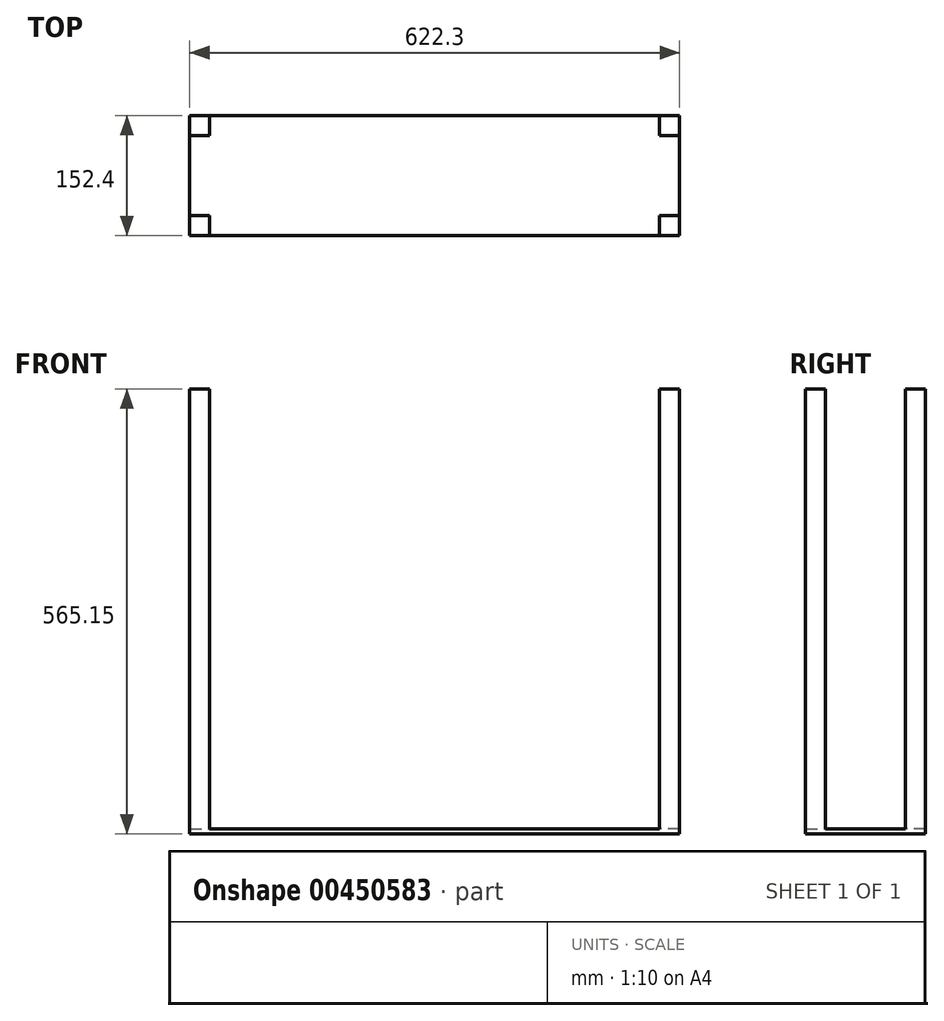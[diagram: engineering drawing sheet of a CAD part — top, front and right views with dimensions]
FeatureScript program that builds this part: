
annotation { "Feature Type Name" : "Feature", "Feature Type Description" : "" }
export const myFeature = defineFeature(function(context is Context, id is Id, definition is map)
    precondition{}
    {
        {
            var Q0;
            Q0=qCreatedBy(makeId("Top.planeOp"),FACE);
            var sketch = newSketch(context, id + "F0", { "sketchPlane" : qUnion([Q0])});
            skLineSegment(sketch, "E0.bottom", {"start": v(311.15, -76.2) * mm, "end": v(-311.15, -76.2) * mm});
            skLineSegment(sketch, "E0.top", {"start": v(311.15, 76.2) * mm, "end": v(-311.15, 76.2) * mm});
            skLineSegment(sketch, "E0.left", {"start": v(311.15, -76.2) * mm, "end": v(311.15, 76.2) * mm});
            skLineSegment(sketch, "E0.right", {"start": v(-311.15, -76.2) * mm, "end": v(-311.15, 76.2) * mm});
            skPoint(sketch, "E0.middle", {"position": v(0, 0) * mm});
            skSolve(sketch);
        }
        {
            var Q0;
            Q0 = qSketchRegion(id + "F0", true);
            extrude(context, id + "F1", {"entities" : qUnion([Q0]), "depth" : 6.35 * mm});
        }
        {
            var Q0;
            Q0=makeQuery(id+"F1.opExtrude","CAP_FACE",FACE,{"disambiguationData":[OSD([sQuery(id+"F0.wireOp",EDGE,"E0.bottom"),sQuery(id+"F0.wireOp",EDGE,"E0.top"),sQuery(id+"F0.wireOp",EDGE,"E0.left"),sQuery(id+"F0.wireOp",EDGE,"E0.right")])],"isStart":false});
            var sketch = newSketch(context, id + "F2", { "sketchPlane" : qUnion([Q0])});
            skLineSegment(sketch, "E1", {"start": v(0, 106.88) * mm, "end": v(0, -98.48) * mm, "construction": true});
            skPoint(sketch, "E1.startSnap0", {"position": v(0, 76.2) * mm});
            skLineSegment(sketch, "E2", {"start": v(-311.15, 0) * mm, "end": v(331.49, 0) * mm, "construction": true});
            skLineSegment(sketch, "E3.bottom", {"start": v(-311.15, 76.2) * mm, "end": v(-285.75, 76.2) * mm});
            skLineSegment(sketch, "E3.top", {"start": v(-311.15, 50.8) * mm, "end": v(-285.75, 50.8) * mm});
            skLineSegment(sketch, "E3.left", {"start": v(-311.15, 76.2) * mm, "end": v(-311.15, 50.8) * mm});
            skLineSegment(sketch, "E3.right", {"start": v(-285.75, 76.2) * mm, "end": v(-285.75, 50.8) * mm});
            skLineSegment(sketch, "E4.MirrorCS", {"start": v(285.75, 76.2) * mm, "end": v(285.75, 50.8) * mm});
            skLineSegment(sketch, "E5.MirrorCS", {"start": v(311.15, 76.2) * mm, "end": v(285.75, 76.2) * mm});
            skLineSegment(sketch, "E6.MirrorCS", {"start": v(311.15, 76.2) * mm, "end": v(311.15, 50.8) * mm});
            skLineSegment(sketch, "E7.MirrorCS", {"start": v(311.15, 50.8) * mm, "end": v(285.75, 50.8) * mm});
            skLineSegment(sketch, "E8.MirrorCS", {"start": v(-311.15, -50.8) * mm, "end": v(-285.75, -50.8) * mm});
            skLineSegment(sketch, "E9.MirrorCS", {"start": v(-285.75, -76.2) * mm, "end": v(-285.75, -50.8) * mm});
            skLineSegment(sketch, "E10.MirrorCS", {"start": v(-311.15, -76.2) * mm, "end": v(-311.15, -50.8) * mm});
            skLineSegment(sketch, "E11.MirrorCS", {"start": v(-311.15, -76.2) * mm, "end": v(-285.75, -76.2) * mm});
            skLineSegment(sketch, "E12.MirrorCS", {"start": v(285.75, -76.2) * mm, "end": v(285.75, -50.8) * mm});
            skLineSegment(sketch, "E13.MirrorCS", {"start": v(311.15, -76.2) * mm, "end": v(285.75, -76.2) * mm});
            skLineSegment(sketch, "E14.MirrorCS", {"start": v(311.15, -76.2) * mm, "end": v(311.15, -50.8) * mm});
            skLineSegment(sketch, "E15.MirrorCS", {"start": v(311.15, -50.8) * mm, "end": v(285.75, -50.8) * mm});
            skSolve(sketch);
        }
        {
            var Q0;
            Q0 = qSketchRegion(id + "F2", true);
            extrude(context, id + "F3", {"entities" : qUnion([Q0]), "operationType" : NewBodyOperationType.ADD, "depth" : 558.8 * mm});
        }
    });
